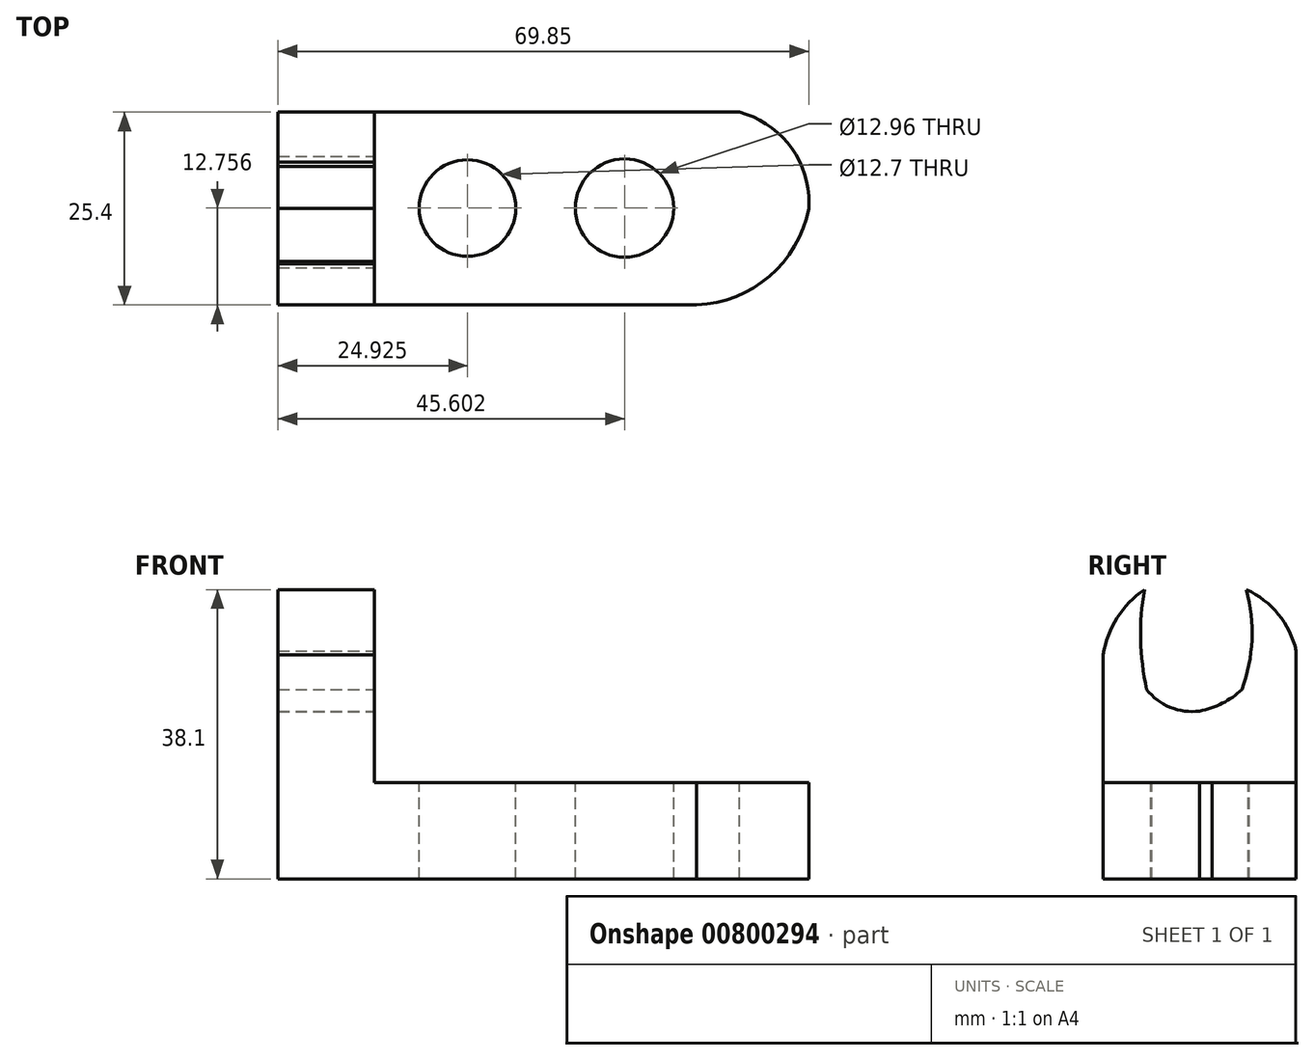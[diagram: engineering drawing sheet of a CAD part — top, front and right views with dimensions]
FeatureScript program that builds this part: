
annotation { "Feature Type Name" : "Feature", "Feature Type Description" : "" }
export const myFeature = defineFeature(function(context is Context, id is Id, definition is map)
    precondition{}
    {
        {
            var Q0;
            Q0=qCreatedBy(makeId("Front.planeOp"),FACE);
            var sketch = newSketch(context, id + "F0", { "sketchPlane" : qUnion([Q0])});
            skLineSegment(sketch, "E0", {"start": v(0, 0) * mm, "end": v(69.85, 0) * mm});
            skLineSegment(sketch, "E1", {"start": v(69.85, 0) * mm, "end": v(69.85, 12.7) * mm});
            skLineSegment(sketch, "E2", {"start": v(69.85, 12.7) * mm, "end": v(12.7, 12.7) * mm});
            skLineSegment(sketch, "E3", {"start": v(12.7, 12.7) * mm, "end": v(12.7, 38.1) * mm});
            skLineSegment(sketch, "E4", {"start": v(12.7, 38.1) * mm, "end": v(0, 38.1) * mm});
            skLineSegment(sketch, "E5", {"start": v(0, 38.1) * mm, "end": v(0, 0) * mm});
            skSolve(sketch);
        }
        {
            var Q0;
            Q0=qSketchRegion(id+"F0",true);
            extrude(context, id + "F1", {"entities" : qUnion([Q0]), "depth" : 25.4 * mm});
        }
        {
            var Q0;
            Q0=makeQuery(id+"F1.opExtrude","SWEPT_FACE",FACE,{"disambiguationData":[OSD([sQuery(id+"F0.wireOp",EDGE,"E2")])]});
            var sketch = newSketch(context, id + "F2", { "sketchPlane" : qUnion([Q0])});
            skArc(sketch, "E6", {"start": v(53.86, -25.4) * mm, "mid": v(64.21, -22.02) * mm, "end": v(69.85, -12.7) * mm});
            skArc(sketch, "E7", {"start": v(69.85, -12.7) * mm, "mid": v(65.42, -2.41) * mm, "end": v(54.48, 0) * mm});
            skSolve(sketch);
        }
        {
            var Q0;
            {var subQ0=sQuery(id+"F2.wireOp",EDGE,"E6");var subQ1=sQuery(id+"F0.wireOp",EDGE,"E2");var subQ4=makeQuery(id+"F1.opExtrude","CAP_EDGE",EDGE,{"disambiguationData":[OSD([subQ1])],"isStart":false});var subQ5=makeQuery(id+"F2.imprint","INTERSECT",VERTEX,{"disambiguationData":[OD(1.0)],"derivedFrom":[subQ4,subQ0]});Q0=makeQuery(id+"F2.imprint","IMPRINT",FACE,{"disambiguationData":[TD([[makeQuery(id+"F2.imprint","IMPRINT",EDGE,{"disambiguationData":[TD([[subQ5,1.0]])],"derivedFrom":subQ4}),-1.0]])]});}
            var Q1;
            {var subQ0=sQuery(id+"F2.wireOp",EDGE,"E7");var subQ1=sQuery(id+"F0.wireOp",EDGE,"E2");var subQ4=makeQuery(id+"F1.opExtrude","CAP_EDGE",EDGE,{"disambiguationData":[OSD([subQ1])],"isStart":true});var subQ5=makeQuery(id+"F2.imprint","INTERSECT",VERTEX,{"disambiguationData":[OD(1.0)],"derivedFrom":[subQ4,subQ0]});Q1=makeQuery(id+"F2.imprint","IMPRINT",FACE,{"disambiguationData":[TD([[makeQuery(id+"F2.imprint","IMPRINT",EDGE,{"disambiguationData":[TD([[subQ5,1.0]])],"derivedFrom":subQ0}),-1.0]])]});}
            extrude(context, id + "F3", {"entities" : qUnion([Q0, Q1]), "operationType" : NewBodyOperationType.REMOVE, "oppositeDirection" : true, "depth" : 25.4 * mm});
        }
        {
            var Q0;
            Q0=makeQuery(id+"F1.opExtrude","SWEPT_FACE",FACE,{"disambiguationData":[OSD([sQuery(id+"F0.wireOp",EDGE,"E3")])]});
            var sketch = newSketch(context, id + "F4", { "sketchPlane" : qUnion([Q0])});
            skArc(sketch, "E8", {"start": v(-7.13, 24.96) * mm, "mid": v(-5.81, 31.48) * mm, "end": v(-6.56, 38.1) * mm});
            skArc(sketch, "E9", {"start": v(-12.7, 22.1) * mm, "mid": v(-9.71, 23.14) * mm, "end": v(-7.13, 24.96) * mm});
            skPoint(sketch, "E9.startSnap0", {"position": v(-12.7, 38.1) * mm});
            skArc(sketch, "E10", {"start": v(-19.97, 38.1) * mm, "mid": v(-20.47, 31.52) * mm, "end": v(-19.68, 24.96) * mm});
            skArc(sketch, "E11", {"start": v(-19.68, 24.96) * mm, "mid": v(-16.57, 22.6) * mm, "end": v(-12.7, 22.1) * mm});
            skSolve(sketch);
        }
        {
            var Q0;
            Q0=qSketchRegion(id+"F4",true);
            var Q1;
            {var subQ1=sQuery(id+"F4.wireOp",EDGE,"E8");Q1=makeQuery(id+"F4.imprint","IMPRINT",FACE,{"disambiguationData":[TD([[makeQuery(id+"F4.imprint","IMPRINT",EDGE,{"derivedFrom":subQ1}),1.0]])]});}
            extrude(context, id + "F5", {"entities" : qUnion([Q0, Q1]), "operationType" : NewBodyOperationType.REMOVE, "oppositeDirection" : true, "depth" : 25.4 * mm});
        }
        {
            var Q0;
            Q0=makeQuery(id+"F1.opExtrude","SWEPT_FACE",FACE,{"disambiguationData":[OSD([sQuery(id+"F0.wireOp",EDGE,"E3")])]});
            var sketch = newSketch(context, id + "F6", { "sketchPlane" : qUnion([Q0])});
            skArc(sketch, "E12", {"start": v(-19.97, 38.1) * mm, "mid": v(-24.53, 32.54) * mm, "end": v(-25.4, 25.4) * mm});
            skArc(sketch, "E13", {"start": v(0, 24.96) * mm, "mid": v(-0.94, 32.7) * mm, "end": v(-6.56, 38.1) * mm});
            skSolve(sketch);
        }
        {
            var Q0;
            Q0=qSketchRegion(id+"F6",true);
            var Q1;
            {var subQ1=sQuery(id+"F0.wireOp",EDGE,"E4");var subQ2=sQuery(id+"F0.wireOp",EDGE,"E3");var subQ3=sQuery(id+"F4.wireOp",EDGE,"E10");var subQ4=makeQuery(id+"F5.boolean.opBoolean","SPLIT",EDGE,{"disambiguationData":[TD([makeQuery(id+"F5.opExtrude","SWEPT_FACE",FACE,{"disambiguationData":[OSD([subQ3])]})])],"derivedFrom":makeQuery(id+"F1.opExtrude","SWEPT_EDGE",EDGE,{"disambiguationData":[OSD([subQ2,subQ1])]})});Q1=makeQuery(id+"F6.imprint","IMPRINT",FACE,{"disambiguationData":[TD([[makeQuery(id+"F6.imprint","IMPRINT",EDGE,{"derivedFrom":subQ4}),-1.0]])]});}
            var Q2;
            {var subQ1=sQuery(id+"F0.wireOp",EDGE,"E4");var subQ2=sQuery(id+"F0.wireOp",EDGE,"E3");var subQ3=sQuery(id+"F4.wireOp",EDGE,"E8");var subQ4=makeQuery(id+"F5.boolean.opBoolean","SPLIT",EDGE,{"disambiguationData":[TD([makeQuery(id+"F5.opExtrude","SWEPT_FACE",FACE,{"disambiguationData":[OSD([subQ3])]})])],"derivedFrom":makeQuery(id+"F1.opExtrude","SWEPT_EDGE",EDGE,{"disambiguationData":[OSD([subQ2,subQ1])]})});Q2=makeQuery(id+"F6.imprint","IMPRINT",FACE,{"disambiguationData":[TD([[makeQuery(id+"F6.imprint","IMPRINT",EDGE,{"derivedFrom":subQ4}),-1.0]])]});}
            extrude(context, id + "F7", {"entities" : qUnion([Q0, Q1, Q2]), "operationType" : NewBodyOperationType.REMOVE, "oppositeDirection" : true, "depth" : 25.4 * mm});
        }
        {
            var Q0;
            {var subQ0=sQuery(id+"F0.wireOp",EDGE,"E2");var subQ1=makeQuery(id+"F1.opExtrude","SWEPT_EDGE",EDGE,{"disambiguationData":[OSD([subQ0,sQuery(id+"F0.wireOp",EDGE,"E3")])]});Q0=makeQuery(id+"F2.imprint","IMPRINT",FACE,{"disambiguationData":[TD([[makeQuery(id+"F2.imprint","IMPRINT",EDGE,{"derivedFrom":subQ1}),-1.0]])]});}
            var sketch = newSketch(context, id + "F8", { "sketchPlane" : qUnion([Q0])});
            skCircle(sketch, "E14", {"center": v(24.92, -12.64) * mm, "radius": 6.35 * mm});
            skCircle(sketch, "E15", {"center": v(45.6, -12.64) * mm, "radius": 6.48 * mm});
            skSolve(sketch);
        }
        {
            var Q0;
            Q0=qSketchRegion(id+"F8",true);
            extrude(context, id + "F9", {"entities" : qUnion([Q0]), "operationType" : NewBodyOperationType.REMOVE, "oppositeDirection" : true, "depth" : 25.4 * mm});
        }
    });
